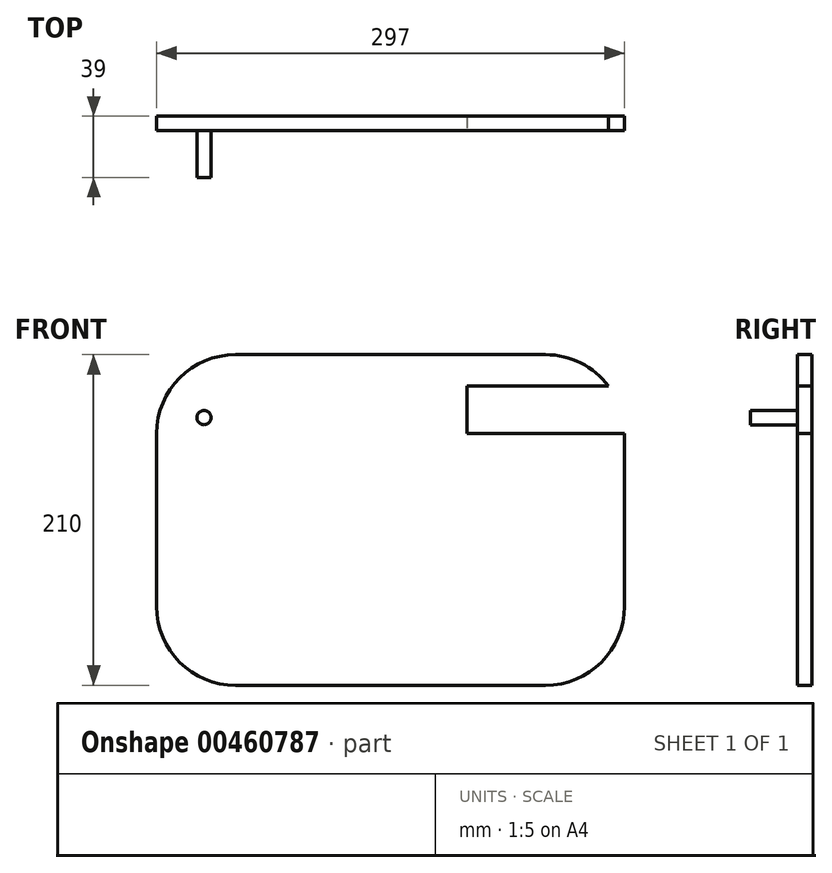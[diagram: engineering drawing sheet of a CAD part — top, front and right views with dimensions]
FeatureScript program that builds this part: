
annotation { "Feature Type Name" : "Feature", "Feature Type Description" : "" }
export const myFeature = defineFeature(function(context is Context, id is Id, definition is map)
    precondition{}
    {
        {
            var Q0;
            Q0=qCreatedBy(makeId("Front.planeOp"),FACE);
            var sketch = newSketch(context, id + "F0", { "sketchPlane" : qUnion([Q0])});
            skLineSegment(sketch, "E0.bottom", {"start": v(-84.54, 109.34) * mm, "end": v(112.46, 109.34) * mm});
            skLineSegment(sketch, "E0.top", {"start": v(-84.54, -100.66) * mm, "end": v(112.46, -100.66) * mm});
            skLineSegment(sketch, "E0.left", {"start": v(-134.54, 59.34) * mm, "end": v(-134.54, -50.66) * mm});
            skLineSegment(sketch, "E0.right", {"start": v(162.46, 59.34) * mm, "end": v(162.46, -50.66) * mm});
            skPoint(sketch, "E1.visualSharp", {"position": v(-134.54, 109.34) * mm});
            skArc(sketch, "E1.filletArc", {"start": v(-84.54, 109.34) * mm, "mid": v(-119.9, 94.7) * mm, "end": v(-134.54, 59.34) * mm});
            skPoint(sketch, "E2.visualSharp", {"position": v(162.46, -100.66) * mm});
            skArc(sketch, "E2.filletArc", {"start": v(112.46, -100.66) * mm, "mid": v(147.82, -86.01) * mm, "end": v(162.46, -50.66) * mm});
            skPoint(sketch, "E3.visualSharp", {"position": v(-134.54, -100.66) * mm});
            skArc(sketch, "E3.filletArc", {"start": v(-134.54, -50.66) * mm, "mid": v(-119.9, -86.01) * mm, "end": v(-84.54, -100.66) * mm});
            skPoint(sketch, "E4.visualSharp", {"position": v(162.46, 109.34) * mm});
            skArc(sketch, "E4.filletArc", {"start": v(162.46, 59.34) * mm, "mid": v(147.82, 94.7) * mm, "end": v(112.46, 109.34) * mm});
            skSolve(sketch);
        }
        {
            var Q0;
            Q0=makeQuery(id+"F0.imprint","IMPRINT",FACE,{"disambiguationData":[TD([[makeQuery(id+"F0.imprint","IMPRINT",EDGE,{"derivedFrom":sQuery(id+"F0.wireOp",EDGE,"E0.bottom")}),-1.0]])]});
            extrude(context, id + "F1", {"entities" : qUnion([Q0]), "depth" : 9 * mm});
        }
        {
            var Q0;
            Q0=makeQuery(id+"F1.opExtrude","CAP_FACE",FACE,{"disambiguationData":[OSD([sQuery(id+"F0.wireOp",EDGE,"E0.bottom"),sQuery(id+"F0.wireOp",EDGE,"E0.top"),sQuery(id+"F0.wireOp",EDGE,"E0.left"),sQuery(id+"F0.wireOp",EDGE,"E0.right"),sQuery(id+"F0.wireOp",EDGE,"E1.filletArc"),sQuery(id+"F0.wireOp",EDGE,"E2.filletArc"),sQuery(id+"F0.wireOp",EDGE,"E3.filletArc"),sQuery(id+"F0.wireOp",EDGE,"E4.filletArc")])],"isStart":false});
            var sketch = newSketch(context, id + "F2", { "sketchPlane" : qUnion([Q0])});
            skCircle(sketch, "E5", {"center": v(-59.54, 69.34) * mm, "radius": 4.5 * mm});
            skCircle(sketch, "E6", {"center": v(-104.54, 69.34) * mm, "radius": 4.5 * mm});
            skSolve(sketch);
        }
        {
            var Q0;
            Q0=makeQuery(id+"F2.imprint","IMPRINT",FACE,{"disambiguationData":[TD([[makeQuery(id+"F2.imprint","IMPRINT",EDGE,{"derivedFrom":sQuery(id+"F2.wireOp",EDGE,"E6")}),1.0]])]});
            extrude(context, id + "F3", {"entities" : qUnion([Q0]), "operationType" : NewBodyOperationType.ADD, "depth" : 30 * mm});
        }
        {
            var Q0;
            Q0=sQuery(id+"F2.wireOp",EDGE,"E5");
            extrude(context, id + "F4", {"bodyType" : ToolBodyType.SURFACE, "surfaceEntities" : qUnion([Q0]), "depth" : 30 * mm});
        }
        {
            var Q0;
            Q0=makeQuery(id+"F1.opExtrude","CAP_FACE",FACE,{"disambiguationData":[OSD([sQuery(id+"F0.wireOp",EDGE,"E0.bottom"),sQuery(id+"F0.wireOp",EDGE,"E0.top"),sQuery(id+"F0.wireOp",EDGE,"E0.left"),sQuery(id+"F0.wireOp",EDGE,"E0.right"),sQuery(id+"F0.wireOp",EDGE,"E1.filletArc"),sQuery(id+"F0.wireOp",EDGE,"E2.filletArc"),sQuery(id+"F0.wireOp",EDGE,"E3.filletArc"),sQuery(id+"F0.wireOp",EDGE,"E4.filletArc")])],"isStart":false});
            var sketch = newSketch(context, id + "F5", { "sketchPlane" : qUnion([Q0])});
            skLineSegment(sketch, "E7.bottom", {"start": v(62.46, 89.34) * mm, "end": v(162.46, 89.34) * mm});
            skLineSegment(sketch, "E7.top", {"start": v(62.46, 59.34) * mm, "end": v(162.46, 59.34) * mm});
            skLineSegment(sketch, "E7.left", {"start": v(62.46, 89.34) * mm, "end": v(62.46, 59.34) * mm});
            skLineSegment(sketch, "E7.right", {"start": v(162.46, 89.34) * mm, "end": v(162.46, 59.34) * mm});
            skSolve(sketch);
        }
        {
            var Q0;
            Q0 = qSketchRegion(id + "F5", true);
            extrude(context, id + "F6", {"entities" : qUnion([Q0]), "operationType" : NewBodyOperationType.REMOVE, "oppositeDirection" : true, "depth" : 25 * mm});
        }
    });
